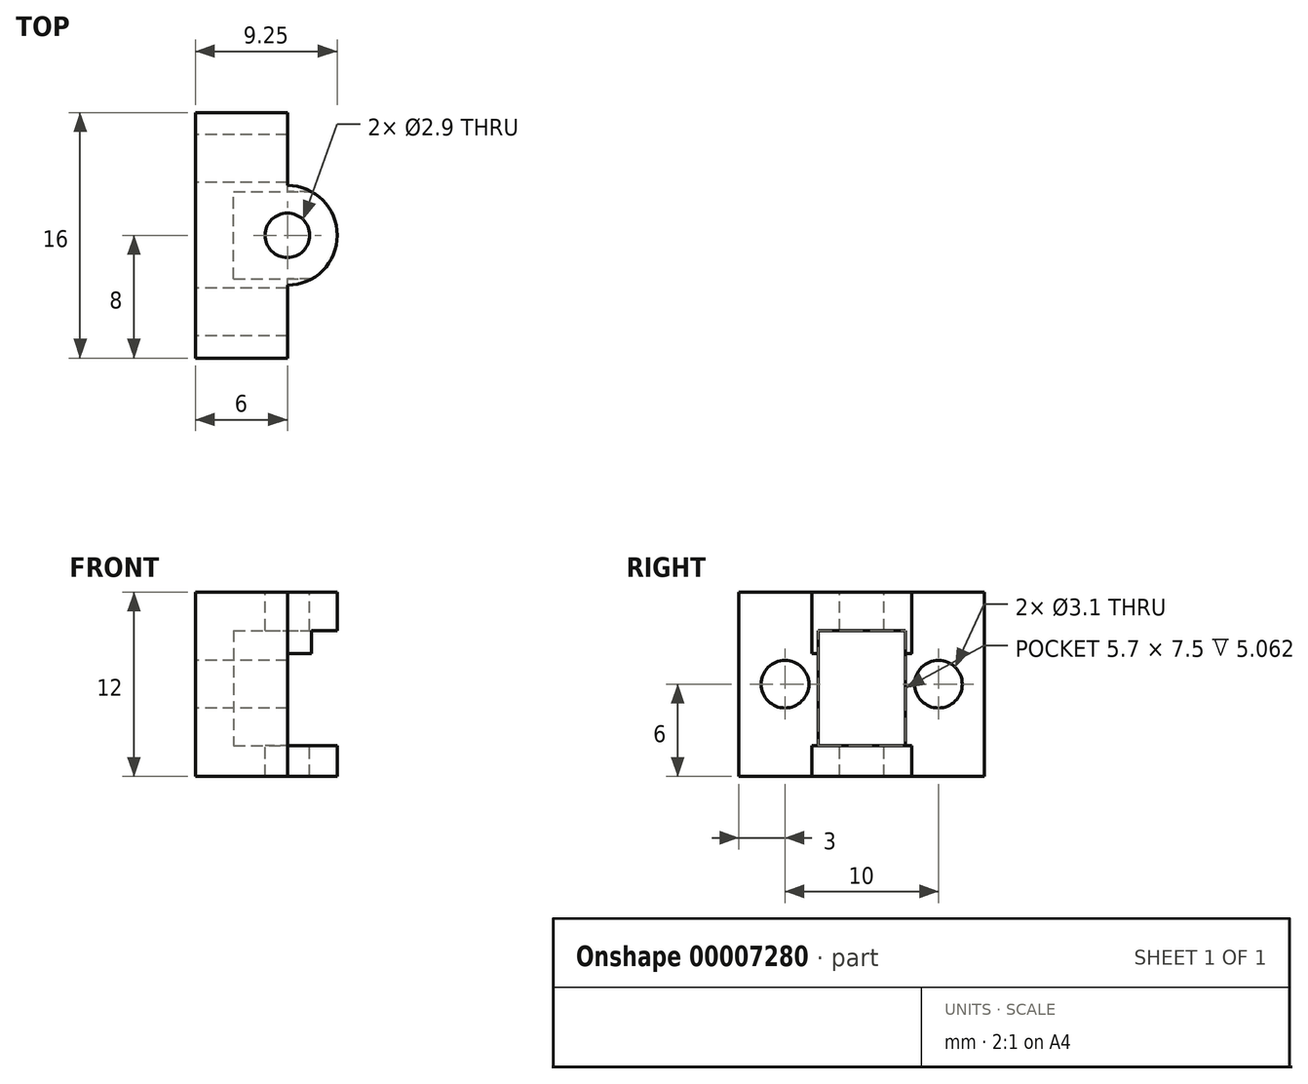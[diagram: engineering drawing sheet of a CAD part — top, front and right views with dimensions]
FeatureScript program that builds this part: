
annotation { "Feature Type Name" : "Feature", "Feature Type Description" : "" }
export const myFeature = defineFeature(function(context is Context, id is Id, definition is map)
    precondition{}
    {
        {
            var Q0;
            Q0=qCreatedBy(makeId("Top.planeOp"),FACE);
            var sketch = newSketch(context, id + "F0", { "sketchPlane" : qUnion([Q0])});
            skLineSegment(sketch, "E0", {"start": v(-6, 0) * mm, "end": v(-6, -8) * mm});
            skLineSegment(sketch, "E1", {"start": v(-6, -8) * mm, "end": v(0, -8) * mm});
            skLineSegment(sketch, "E2", {"start": v(0, -8) * mm, "end": v(0, -3.25) * mm});
            skArc(sketch, "E3", {"start": v(0, -3.25) * mm, "mid": v(2.3, -2.3) * mm, "end": v(3.25, 0) * mm});
            skArc(sketch, "E4.0.MirrorCS", {"start": v(0, 3.25) * mm, "mid": v(2.3, 2.3) * mm, "end": v(3.25, 0) * mm});
            skLineSegment(sketch, "E4.1.MirrorCS", {"start": v(0, 8) * mm, "end": v(0, 3.25) * mm});
            skLineSegment(sketch, "E4.2.MirrorCS", {"start": v(-6, 0) * mm, "end": v(-6, 8) * mm});
            skLineSegment(sketch, "E4.3.MirrorCS", {"start": v(-6, 8) * mm, "end": v(0, 8) * mm});
            skSolve(sketch);
        }
        {
            var Q0;
            Q0=makeQuery(id+"F0.imprint","IMPRINT",FACE,{"disambiguationData":[TD([[makeQuery(id+"F0.imprint","IMPRINT",EDGE,{"derivedFrom":sQuery(id+"F0.wireOp",EDGE,"E0")}),1.0]])]});
            extrude(context, id + "F1", {"entities" : qUnion([Q0]), "depth" : 12 * mm});
        }
        {
            var Q0;
            Q0=makeQuery(id+"F1.opExtrude","CAP_FACE",FACE,{"disambiguationData":[OSD([sQuery(id+"F0.wireOp",EDGE,"E0"),sQuery(id+"F0.wireOp",EDGE,"E1"),sQuery(id+"F0.wireOp",EDGE,"E2"),sQuery(id+"F0.wireOp",EDGE,"E3"),sQuery(id+"F0.wireOp",EDGE,"E4.0.MirrorCS"),sQuery(id+"F0.wireOp",EDGE,"E4.1.MirrorCS"),sQuery(id+"F0.wireOp",EDGE,"E4.2.MirrorCS"),sQuery(id+"F0.wireOp",EDGE,"E4.3.MirrorCS")])],"isStart":false});
            var sketch = newSketch(context, id + "F2", { "sketchPlane" : qUnion([Q0])});
            skCircle(sketch, "E5", {"center": v(0, 0) * mm, "radius": 1.45 * mm});
            skSolve(sketch);
        }
        {
            var Q0;
            Q0=makeQuery(id+"F2.imprint","IMPRINT",FACE,{"disambiguationData":[TD([[makeQuery(id+"F2.imprint","IMPRINT",EDGE,{"derivedFrom":sQuery(id+"F2.wireOp",EDGE,"E5")}),1.0]])]});
            extrude(context, id + "F3", {"entities" : qUnion([Q0]), "operationType" : NewBodyOperationType.REMOVE, "endBound" : BoundingType.THROUGH_ALL, "oppositeDirection" : true, "depth" : 25 * mm});
        }
        {
            var Q0;
            Q0=makeQuery(id+"F1.opExtrude","SWEPT_FACE",FACE,{"disambiguationData":[OSD([sQuery(id+"F0.wireOp",EDGE,"E0"),sQuery(id+"F0.wireOp",EDGE,"E4.2.MirrorCS")])]});
            var sketch = newSketch(context, id + "F4", { "sketchPlane" : qUnion([Q0])});
            skCircle(sketch, "E6", {"center": v(-5, 6) * mm, "radius": 1.55 * mm});
            skCircle(sketch, "E7", {"center": v(5, 6) * mm, "radius": 1.55 * mm});
            skLineSegment(sketch, "E8", {"start": v(0, 12) * mm, "end": v(0, 0) * mm, "construction": true});
            skLineSegment(sketch, "E9", {"start": v(-5, 6) * mm, "end": v(5, 6) * mm, "construction": true});
            skSolve(sketch);
        }
        {
            var Q0;
            Q0 = qSketchRegion(id + "F4", true);
            extrude(context, id + "F5", {"entities" : qUnion([Q0]), "operationType" : NewBodyOperationType.REMOVE, "endBound" : BoundingType.THROUGH_ALL, "oppositeDirection" : true, "depth" : 25 * mm});
        }
        {
            var Q0;
            Q0=makeQuery(id+"F1.opExtrude","SWEPT_FACE",FACE,{"disambiguationData":[OSD([sQuery(id+"F0.wireOp",EDGE,"E2")])]});
            var sketch = newSketch(context, id + "F6", { "sketchPlane" : qUnion([Q0])});
            skLineSegment(sketch, "E10.bottom", {"start": v(-13.32, 8) * mm, "end": v(13.7, 8) * mm});
            skLineSegment(sketch, "E10.top", {"start": v(-13.32, 2) * mm, "end": v(13.7, 2) * mm});
            skLineSegment(sketch, "E10.left", {"start": v(-13.32, 8) * mm, "end": v(-13.32, 2) * mm});
            skLineSegment(sketch, "E10.right", {"start": v(13.7, 8) * mm, "end": v(13.7, 2) * mm});
            skSolve(sketch);
        }
        {
            var Q0;
            Q0 = qSketchRegion(id + "F6", true);
            var Q1;
            Q1=sQuery(id+"F6.wireOp",EDGE,"31d32c9c-989d-4857-90ea-1581f7af95df");
            var Q2;
            Q2=sQuery(id+"F6.wireOp",EDGE,"d3e62f8c-c4f7-48d4-9b93-d89b6259e490");
            extrude(context, id + "F7", {"entities" : qUnion([Q0]), "operationType" : NewBodyOperationType.REMOVE, "surfaceEntities" : qUnion([Q1, Q2]), "endBound" : BoundingType.THROUGH_ALL, "depth" : 25 * mm});
        }
        {
            var Q0;
            Q0=qCreatedBy(makeId("Right.planeOp"),FACE);
            var sketch = newSketch(context, id + "F8", { "sketchPlane" : qUnion([Q0])});
            skLineSegment(sketch, "E11.bottom", {"start": v(-2.85, 9.5) * mm, "end": v(2.85, 9.5) * mm});
            skLineSegment(sketch, "E11.top", {"start": v(-2.85, 2) * mm, "end": v(2.85, 2) * mm});
            skLineSegment(sketch, "E11.left", {"start": v(-2.85, 9.5) * mm, "end": v(-2.85, 2) * mm});
            skLineSegment(sketch, "E11.right", {"start": v(2.85, 9.5) * mm, "end": v(2.85, 2) * mm});
            skLineSegment(sketch, "E12", {"start": v(0, 0) * mm, "end": v(0, 6.4) * mm, "construction": true});
            skSolve(sketch);
        }
        {
            var Q0;
            Q0 = qSketchRegion(id + "F8", true);
            extrude(context, id + "F9", {"entities" : qUnion([Q0]), "operationType" : NewBodyOperationType.REMOVE, "oppositeDirection" : true, "depth" : 3.5 * mm});
        }
        {
            var Q0;
            Q0 = qSketchRegion(id + "F8", true);
            extrude(context, id + "F10", {"entities" : qUnion([Q0]), "operationType" : NewBodyOperationType.REMOVE, "endBound" : BoundingType.THROUGH_ALL, "depth" : 25 * mm});
        }
    });
